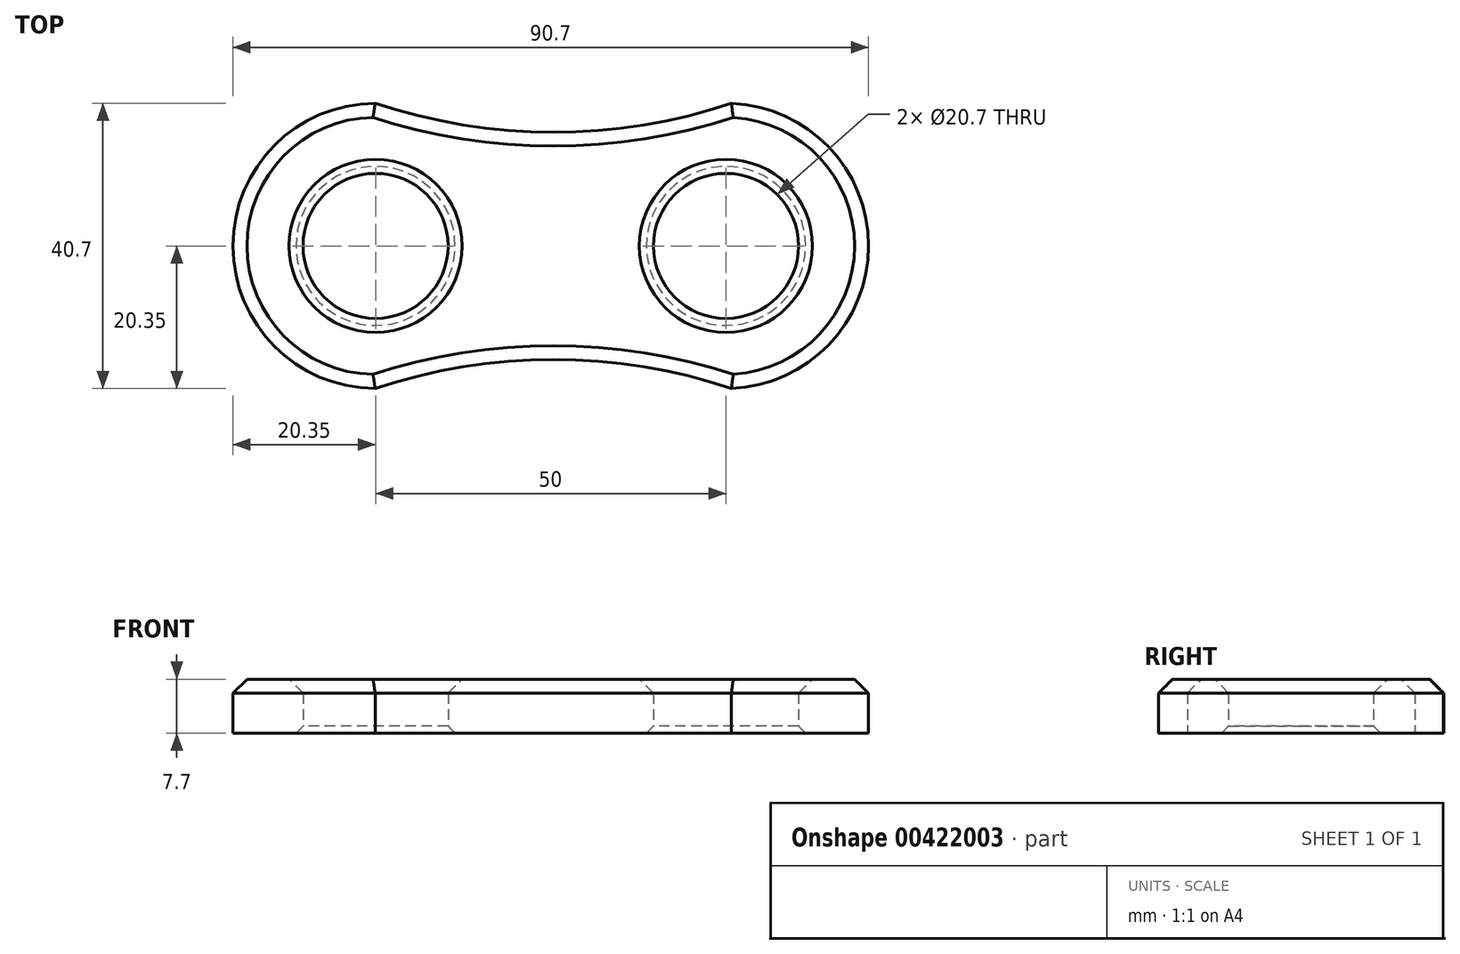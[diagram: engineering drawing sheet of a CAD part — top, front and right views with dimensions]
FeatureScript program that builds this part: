
annotation { "Feature Type Name" : "Feature", "Feature Type Description" : "" }
export const myFeature = defineFeature(function(context is Context, id is Id, definition is map)
    precondition{}
    {
        {
            var Q0;
            Q0=qCreatedBy(makeId("Top.planeOp"),FACE);
            var sketch = newSketch(context, id + "F0", { "sketchPlane" : qUnion([Q0])});
            skLineSegment(sketch, "E0", {"start": v(0, 0) * mm, "end": v(25, 0) * mm});
            skLineSegment(sketch, "E1", {"start": v(0, 0) * mm, "end": v(-25, 0) * mm});
            skCircle(sketch, "E2", {"center": v(-25, 0) * mm, "radius": 10.35 * mm});
            skCircle(sketch, "E3", {"center": v(25, 0) * mm, "radius": 10.35 * mm});
            skCircle(sketch, "E4.0", {"center": v(-25, 0) * mm, "radius": 20.35 * mm});
            skCircle(sketch, "E5.0", {"center": v(25, 0) * mm, "radius": 20.35 * mm});
            skArc(sketch, "E6", {"start": v(-25.05, 20.35) * mm, "mid": v(0.35, 16.23) * mm, "end": v(25.76, 20.34) * mm});
            skArc(sketch, "E7.MirrorCS", {"start": v(-25.05, -20.35) * mm, "mid": v(0.35, -16.23) * mm, "end": v(25.76, -20.34) * mm});
            skSolve(sketch);
        }
        {
            var Q0;
            Q0=makeQuery(id+"F0.imprint","IMPRINT",FACE,{"disambiguationData":[TD([[makeQuery(id+"F0.imprint","IMPRINT",EDGE,{"derivedFrom":sQuery(id+"F0.wireOp",EDGE,"E2")}),-1.0]])]});
            var Q1;
            {var subQ1=sQuery(id+"F0.wireOp",EDGE,"E1");var subQ7=sQuery(id+"F0.wireOp",EDGE,"E0");var subQ8=makeQuery(id+"F0.imprint","INTERSECT",VERTEX,{"derivedFrom":[subQ7,subQ1]});Q1=makeQuery(id+"F0.imprint","IMPRINT",FACE,{"disambiguationData":[TD([[makeQuery(id+"F0.imprint","IMPRINT",EDGE,{"disambiguationData":[TD([[subQ8,-1.0]])],"derivedFrom":subQ7}),1.0]])]});}
            var Q2;
            {var subQ1=sQuery(id+"F0.wireOp",EDGE,"E1");var subQ6=sQuery(id+"F0.wireOp",EDGE,"E0");var subQ9=makeQuery(id+"F0.imprint","INTERSECT",VERTEX,{"derivedFrom":[subQ6,subQ1]});Q2=makeQuery(id+"F0.imprint","IMPRINT",FACE,{"disambiguationData":[TD([[makeQuery(id+"F0.imprint","IMPRINT",EDGE,{"disambiguationData":[TD([[subQ9,-1.0]])],"derivedFrom":subQ6}),-1.0]])]});}
            var Q3;
            Q3=makeQuery(id+"F0.imprint","IMPRINT",FACE,{"disambiguationData":[TD([[makeQuery(id+"F0.imprint","IMPRINT",EDGE,{"derivedFrom":sQuery(id+"F0.wireOp",EDGE,"E3")}),-1.0]])]});
            extrude(context, id + "F1", {"entities" : qUnion([Q0, Q1, Q2, Q3]), "depth" : 7.7 * mm});
        }
        {
            var Q0;
            Q0=makeQuery(id+"F1.opExtrude","CAP_FACE",FACE,{"disambiguationData":[OSD([sQuery(id+"F0.wireOp",EDGE,"E2"),sQuery(id+"F0.wireOp",EDGE,"E3"),sQuery(id+"F0.wireOp",EDGE,"E4.0"),sQuery(id+"F0.wireOp",EDGE,"E5.0"),sQuery(id+"F0.wireOp",EDGE,"E6"),sQuery(id+"F0.wireOp",EDGE,"E7.MirrorCS")])],"isStart":false});
            chamfer(context, id + "F2", {"entities" : qUnion([Q0]), "width" : 2 * mm, "tangentPropagation" : true});
        }
        {
            var Q0;
            Q0=makeQuery(id+"F1.opExtrude","CAP_EDGE",EDGE,{"disambiguationData":[OSD([sQuery(id+"F0.wireOp",EDGE,"E2")])],"isStart":true});
            var Q1;
            Q1=makeQuery(id+"F1.opExtrude","CAP_EDGE",EDGE,{"disambiguationData":[OSD([sQuery(id+"F0.wireOp",EDGE,"E3")])],"isStart":true});
            chamfer(context, id + "F3", {"entities" : qUnion([Q0, Q1]), "width" : 1 * mm, "tangentPropagation" : true});
        }
    });
